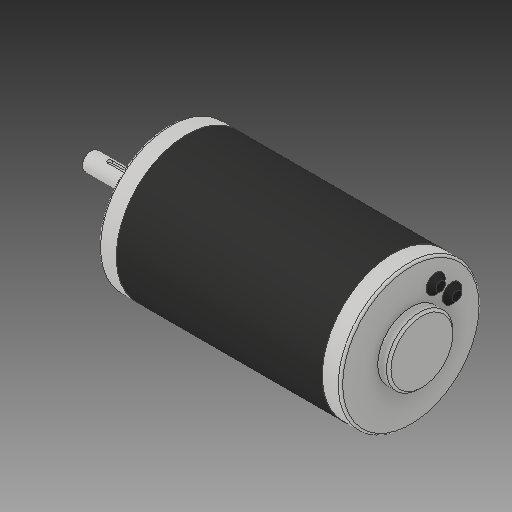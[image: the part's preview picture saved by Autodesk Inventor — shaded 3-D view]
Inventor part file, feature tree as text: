
AUTODESK INVENTOR PART (.ipt)
format: ipt  version: 2018 (Build 220112000, 112)  size: 166,400 bytes
history: native  units: in
note: dims shown in document units (in); Inventor stores cm internally (conversion verified against a paired STEP export)
features: chamfer x1
ambient origin geometry x8: Origin, YZ Plane, XZ Plane, XY Plane, X Axis, Y Axis, Z Axis, Center Point
bodies: Solid1 (feature_tree)
feature tree (1):
  chamfer  "Chamfer3"  [1 undecoded]
note: 1 required parameter value undecoded (feature->parameter linkage not recoverable at this tier; creation-order binding heuristic only, values carry confidence <= 0.55)
